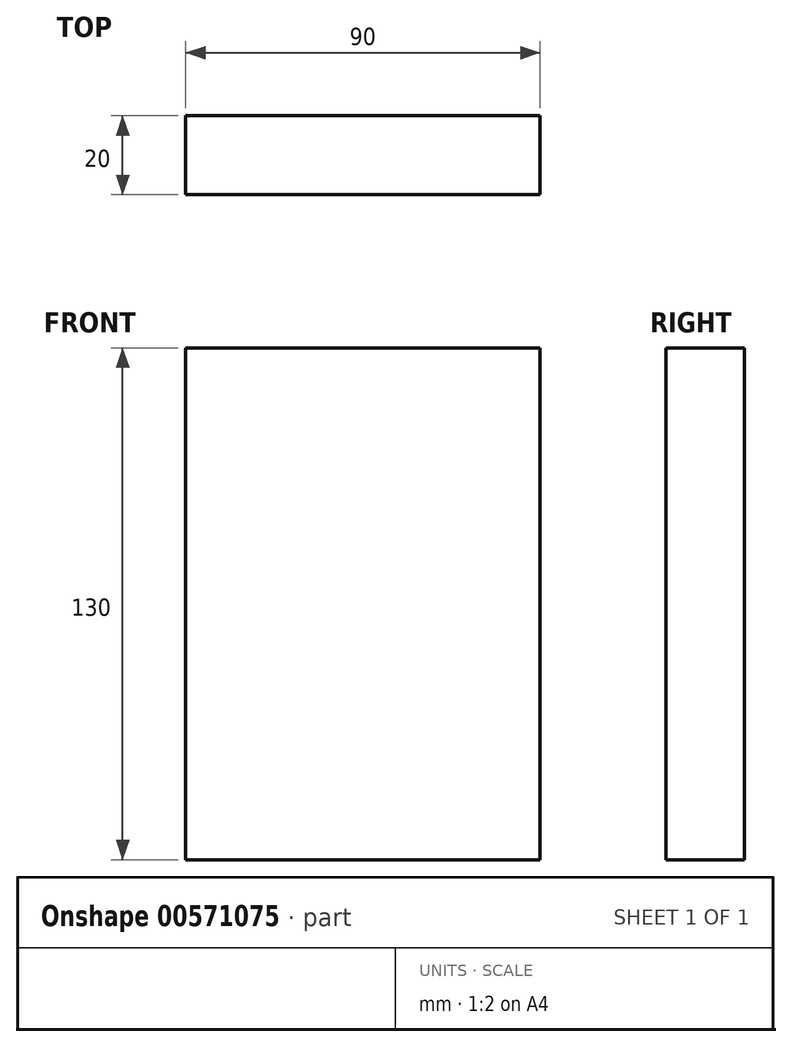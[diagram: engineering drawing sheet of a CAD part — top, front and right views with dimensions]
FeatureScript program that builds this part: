
annotation { "Feature Type Name" : "Feature", "Feature Type Description" : "" }
export const myFeature = defineFeature(function(context is Context, id is Id, definition is map)
    precondition{}
    {
        {
            var Q0;
            Q0=qCreatedBy(makeId("Front.planeOp"),FACE);
            var sketch = newSketch(context, id + "F0", { "sketchPlane" : qUnion([Q0])});
            skLineSegment(sketch, "E0.bottom", {"start": v(45, 65) * mm, "end": v(-45, 65) * mm});
            skLineSegment(sketch, "E0.top", {"start": v(45, -65) * mm, "end": v(-45, -65) * mm});
            skLineSegment(sketch, "E0.left", {"start": v(45, 65) * mm, "end": v(45, -65) * mm});
            skLineSegment(sketch, "E0.right", {"start": v(-45, 65) * mm, "end": v(-45, -65) * mm});
            skPoint(sketch, "E0.middle", {"position": v(0, 0) * mm});
            skSolve(sketch);
        }
        {
            var Q0;
            Q0 = qSketchRegion(id + "F0", true);
            extrude(context, id + "F1", {"entities" : qUnion([Q0]), "endBound" : BoundingType.SYMMETRIC, "depth" : 20 * mm, "offsetDistance" : 25 * mm});
        }
    });
